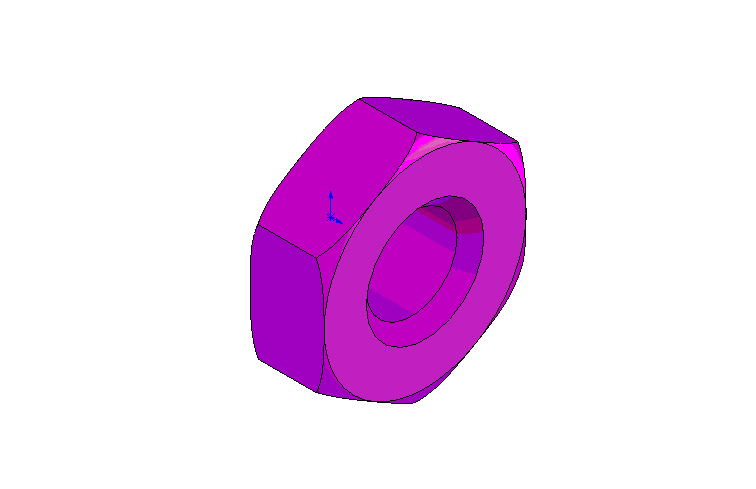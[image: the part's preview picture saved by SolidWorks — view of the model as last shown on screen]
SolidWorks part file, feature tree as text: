
SOLIDWORKS PART (.sldprt)
format: sldprt  version: not decoded by parser v0  size: 272,384 bytes
history: native  units: mm
features: sketch x4, plane x3, cut_revolve x2, material x1, extrude x1, cut_extrude x1, chamfer x1 (+10 scaffold rows collapsed)
feature tree (23):
  scaffold x10  (default folders/planes/origin — collapsed)
  material  "Matériau <non spécifié>"
  plane  "Plan de face"
  plane  "Plan de dessus"
  plane  "Plan de droite"
  sketch  "Esquisse1"  dims[D1=15.0mm]
  extrude  "Extrusion1"  Depth=7mm
  sketch  "Esquisse2"  dims[D1=13.5mm D2=1.5mm]
  cut_revolve  "Enlèvement de matière-Révolution1"  Angle=360deg
  sketch  "Esquisse3"  dims[D1=6.75mm]
  cut_extrude  "Enlèv. mat.-Extru.1"  [1 undecoded]
  chamfer  "Chanfrein1"  Distance=1mm Angle=45deg
  sketch  "Esquisse4"  dims[D1=2.0mm D2=15.0mm D3=0.6mm]
  cut_revolve  "Enlèvement de matière-Révolution2"  Angle=360deg
decode coverage: 8 of 9 modeling features carry decoded parameters
note: 1 parameter value undecoded
note: suppression state not decoded; provenance and decode notes live in map.json
